# Revit family: 32_Berkvens_Berdo BA std + Berklon opdek (Vrij plaatsen)
name_source: partatom
category: Doors
units: mm (PartAtom-declared; Revit-internal decimal feet)

## family parameters
Always vertical = No
Cut with Voids When Loaded = No
Room Calculation Point = No
Shared = No
Work Plane-Based = No

## types (3) — shared parameters
60_45 Model kozijn = BA enkeldeurs
60_63 Vloerplafondhoogte = 2650 mm  [stored 8.69423 ft]
60_81 Uitvoering kozijn = Bovenlicht afgeslankte bovendorpel
60_84 Type kozijn = Berdo stalen montagekozijn
70_88 Uitvoering deur = standaard
70_90 Type deur = Berklon, lakdeur
80_60 Kantuitvoering = opdek
80_75 Deurhoogte = 2315 mm  [stored 7.59514 ft]
Analytic Construction = <None>
Assembly Code = 32.31
Compartmentation = No
FireExit = No
IsExternal = No
M1 = Berkvens_-maak keuze-
M2 = Berkvens gebroken wit
M3 = Berkvens_reinwit
M4 = Berkvens_kristalwit
M5 = Berkvens_-maak keuze-
M6 = Berkvens_-maak keuze-
Manufacturer = Berkvens
Model = Berdo BA
SelfClosing = No
SmokeStop = No
URL = www.berkvens.nl
Versie = 1.0

## per-type parameters (varying)
| type | 60_51 Sparingsmaat | 80_90 Deurbreedte actieve deur |
| 930x2315 | 975 mm  [stored 3.19882 ft] | 930 mm  [stored 3.05118 ft] |
| 730x2315 | 775 mm  [stored 2.54265 ft] | 730 mm  [stored 2.39501 ft] |
| 880x2315 | 925 mm  [stored 3.03478 ft] | 880 mm  [stored 2.88714 ft] |

note: [stored X ft] marks values corroborated as IEEE doubles in the binary element streams (Revit-internal decimal feet)

## geometry (parser evidence)
native form markers: Sweep x30
no freeform markers — native parametric forms only
